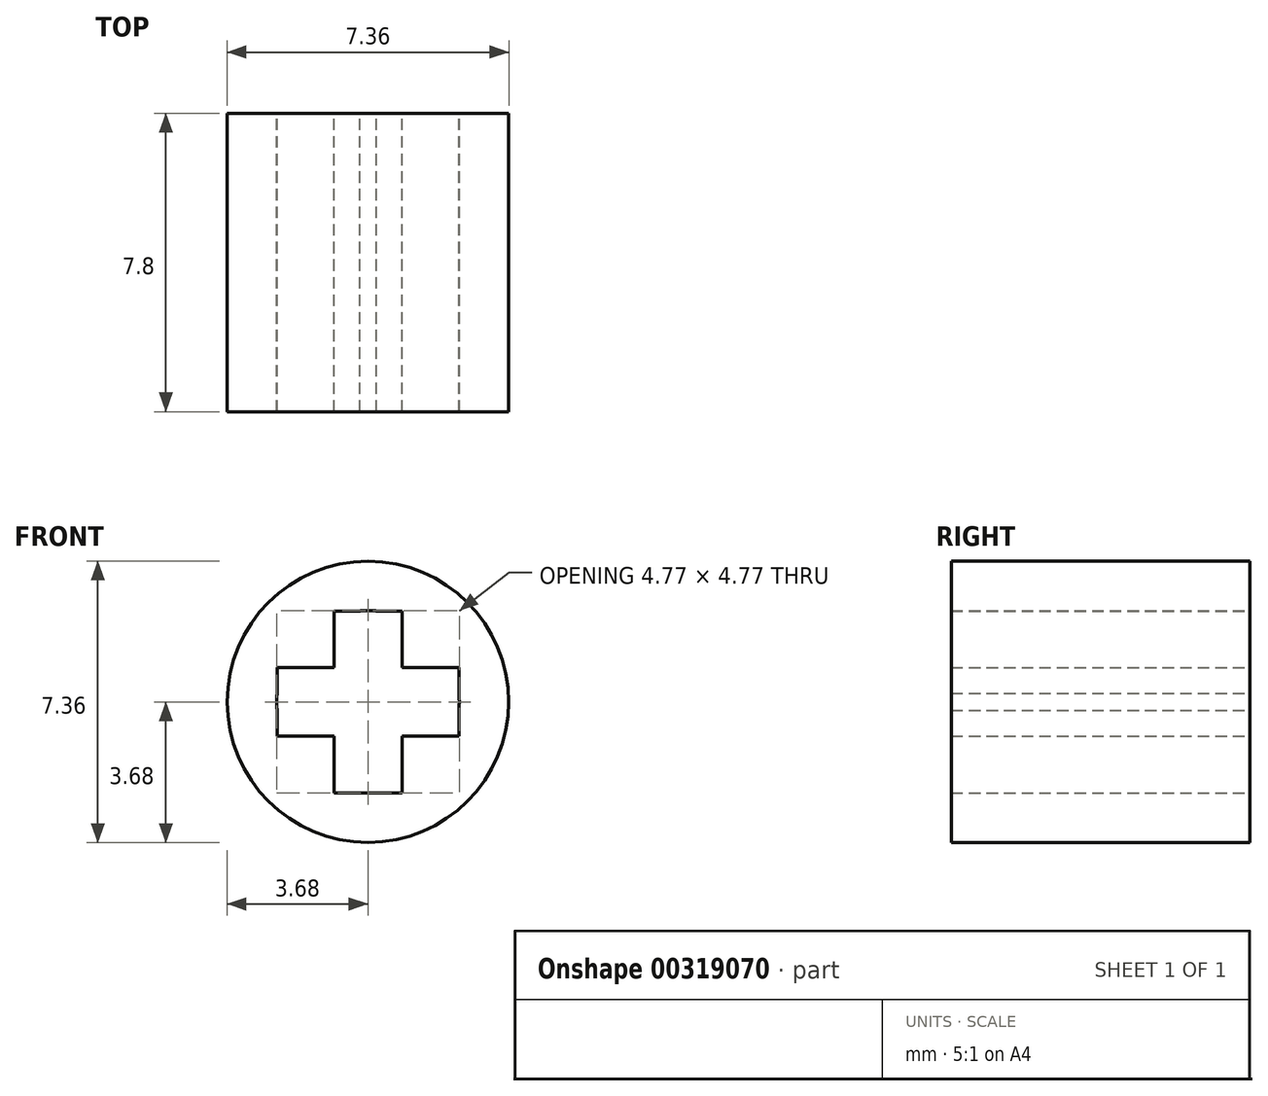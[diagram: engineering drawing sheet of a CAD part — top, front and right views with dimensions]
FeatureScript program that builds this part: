
annotation { "Feature Type Name" : "Feature", "Feature Type Description" : "" }
export const myFeature = defineFeature(function(context is Context, id is Id, definition is map)
    precondition{}
    {
        {
            var Q0;
            Q0=qCreatedBy(makeId("Front.planeOp"),FACE);
            var sketch = newSketch(context, id + "F0", { "sketchPlane" : qUnion([Q0])});
            skCircle(sketch, "E0", {"center": v(0, 0) * mm, "radius": 3.67 * mm});
            skPoint(sketch, "E1", {"position": v(-3.68, 0) * mm});
            skPoint(sketch, "E2", {"position": v(0, -2.38) * mm});
            skLineSegment(sketch, "E3.bottom", {"start": v(-2.38, 0.9) * mm, "end": v(2.38, 0.9) * mm});
            skLineSegment(sketch, "E3.top", {"start": v(-2.38, -0.89) * mm, "end": v(2.38, -0.89) * mm});
            skLineSegment(sketch, "E3.left", {"start": v(-2.38, 0.89) * mm, "end": v(-2.38, -0.89) * mm});
            skLineSegment(sketch, "E3.right", {"start": v(2.38, 0.89) * mm, "end": v(2.38, -0.89) * mm});
            skLineSegment(sketch, "E4", {"start": v(0, 0.89) * mm, "end": v(0, -0.89) * mm});
            skLineSegment(sketch, "E5.bottom", {"start": v(-0.9, 2.38) * mm, "end": v(0.9, 2.38) * mm});
            skLineSegment(sketch, "E5.top", {"start": v(-0.9, -2.37) * mm, "end": v(0.9, -2.37) * mm});
            skLineSegment(sketch, "E5.left", {"start": v(-0.9, 2.37) * mm, "end": v(-0.9, -2.37) * mm});
            skLineSegment(sketch, "E5.right", {"start": v(0.89, 2.37) * mm, "end": v(0.89, -2.37) * mm});
            skLineSegment(sketch, "E6", {"start": v(-0.9, 0) * mm, "end": v(0.9, 0) * mm});
            skCircle(sketch, "E7", {"center": v(0, 0) * mm, "radius": 2.38 * mm});
            skSolve(sketch);
        }
        {
            var Q0;
            Q0=makeQuery(id+"F0.imprint","IMPRINT",FACE,{"disambiguationData":[TD([[makeQuery(id+"F0.imprint","IMPRINT",EDGE,{"derivedFrom":sQuery(id+"F0.wireOp",EDGE,"E0")}),1.0]])]});
            var Q1;
            {var subQ0=sQuery(id+"F0.wireOp",EDGE,"E5.left");var subQ1=sQuery(id+"F0.wireOp",EDGE,"6KHPiTR4-YgFa-hmAh-xzcl-P7OBzmZ2RswI");var subQ2=makeQuery(id+"F0.imprint","INTERSECT",VERTEX,{"disambiguationData":[OD(0.0)],"derivedFrom":[subQ1,subQ0]});Q1=makeQuery(id+"F0.imprint","IMPRINT",FACE,{"disambiguationData":[TD([[makeQuery(id+"F0.imprint","IMPRINT",EDGE,{"disambiguationData":[TD([[subQ2,-1.0]])],"derivedFrom":subQ1}),-1.0]])]});}
            var Q2;
            {var subQ0=sQuery(id+"F0.wireOp",EDGE,"E5.left");var subQ1=sQuery(id+"F0.wireOp",EDGE,"6KHPiTR4-YgFa-hmAh-xzcl-P7OBzmZ2RswI");var subQ2=makeQuery(id+"F0.imprint","INTERSECT",VERTEX,{"disambiguationData":[OD(0.0)],"derivedFrom":[subQ1,subQ0]});Q2=makeQuery(id+"F0.imprint","IMPRINT",FACE,{"disambiguationData":[TD([[makeQuery(id+"F0.imprint","IMPRINT",EDGE,{"disambiguationData":[TD([[subQ2,-1.0]])],"derivedFrom":subQ1}),1.0]])]});}
            var Q3;
            {var subQ0=sQuery(id+"F0.wireOp",EDGE,"E3.left");var subQ1=sQuery(id+"F0.wireOp",EDGE,"6KHPiTR4-YgFa-hmAh-xzcl-P7OBzmZ2RswI");var subQ2=makeQuery(id+"F0.imprint","INTERSECT",VERTEX,{"disambiguationData":[OD(0.0)],"derivedFrom":[subQ1,subQ0]});Q3=makeQuery(id+"F0.imprint","IMPRINT",FACE,{"disambiguationData":[TD([[makeQuery(id+"F0.imprint","IMPRINT",EDGE,{"disambiguationData":[TD([[subQ2,-1.0]])],"derivedFrom":subQ1}),-1.0]])]});}
            var Q4;
            {var subQ0=sQuery(id+"F0.wireOp",EDGE,"E3.left");var subQ1=sQuery(id+"F0.wireOp",EDGE,"6KHPiTR4-YgFa-hmAh-xzcl-P7OBzmZ2RswI");var subQ2=makeQuery(id+"F0.imprint","INTERSECT",VERTEX,{"disambiguationData":[OD(1.0)],"derivedFrom":[subQ1,subQ0]});Q4=makeQuery(id+"F0.imprint","IMPRINT",FACE,{"disambiguationData":[TD([[makeQuery(id+"F0.imprint","IMPRINT",EDGE,{"disambiguationData":[TD([[subQ2,-1.0]])],"derivedFrom":subQ1}),-1.0]])]});}
            var Q5;
            {var subQ0=sQuery(id+"F0.wireOp",EDGE,"E3.top");var subQ1=sQuery(id+"F0.wireOp",EDGE,"6KHPiTR4-YgFa-hmAh-xzcl-P7OBzmZ2RswI");var subQ2=makeQuery(id+"F0.imprint","INTERSECT",VERTEX,{"disambiguationData":[OD(0.0)],"derivedFrom":[subQ1,subQ0]});Q5=makeQuery(id+"F0.imprint","IMPRINT",FACE,{"disambiguationData":[TD([[makeQuery(id+"F0.imprint","IMPRINT",EDGE,{"disambiguationData":[TD([[subQ2,-1.0]])],"derivedFrom":subQ1}),-1.0]])]});}
            var Q6;
            {var subQ0=sQuery(id+"F0.wireOp",EDGE,"E5.top");var subQ1=sQuery(id+"F0.wireOp",EDGE,"6KHPiTR4-YgFa-hmAh-xzcl-P7OBzmZ2RswI");var subQ2=makeQuery(id+"F0.imprint","INTERSECT",VERTEX,{"disambiguationData":[OD(0.0)],"derivedFrom":[subQ1,subQ0]});Q6=makeQuery(id+"F0.imprint","IMPRINT",FACE,{"disambiguationData":[TD([[makeQuery(id+"F0.imprint","IMPRINT",EDGE,{"disambiguationData":[TD([[subQ2,-1.0]])],"derivedFrom":subQ1}),-1.0]])]});}
            var Q7;
            {var subQ0=sQuery(id+"F0.wireOp",EDGE,"E5.top");var subQ1=sQuery(id+"F0.wireOp",EDGE,"6KHPiTR4-YgFa-hmAh-xzcl-P7OBzmZ2RswI");var subQ2=makeQuery(id+"F0.imprint","INTERSECT",VERTEX,{"disambiguationData":[OD(1.0)],"derivedFrom":[subQ1,subQ0]});Q7=makeQuery(id+"F0.imprint","IMPRINT",FACE,{"disambiguationData":[TD([[makeQuery(id+"F0.imprint","IMPRINT",EDGE,{"disambiguationData":[TD([[subQ2,-1.0]])],"derivedFrom":subQ1}),-1.0]])]});}
            var Q8;
            {var subQ0=sQuery(id+"F0.wireOp",EDGE,"E5.right");var subQ1=sQuery(id+"F0.wireOp",EDGE,"6KHPiTR4-YgFa-hmAh-xzcl-P7OBzmZ2RswI");var subQ2=makeQuery(id+"F0.imprint","INTERSECT",VERTEX,{"disambiguationData":[OD(1.0)],"derivedFrom":[subQ1,subQ0]});Q8=makeQuery(id+"F0.imprint","IMPRINT",FACE,{"disambiguationData":[TD([[makeQuery(id+"F0.imprint","IMPRINT",EDGE,{"disambiguationData":[TD([[subQ2,-1.0]])],"derivedFrom":subQ1}),-1.0]])]});}
            var Q9;
            {var subQ0=sQuery(id+"F0.wireOp",EDGE,"E3.right");var subQ1=sQuery(id+"F0.wireOp",EDGE,"6KHPiTR4-YgFa-hmAh-xzcl-P7OBzmZ2RswI");var subQ2=makeQuery(id+"F0.imprint","INTERSECT",VERTEX,{"disambiguationData":[OD(0.0)],"derivedFrom":[subQ1,subQ0]});Q9=makeQuery(id+"F0.imprint","IMPRINT",FACE,{"disambiguationData":[TD([[makeQuery(id+"F0.imprint","IMPRINT",EDGE,{"disambiguationData":[TD([[subQ2,1.0]])],"derivedFrom":subQ1}),-1.0]])]});}
            var Q10;
            {var subQ0=sQuery(id+"F0.wireOp",EDGE,"E3.bottom");var subQ1=sQuery(id+"F0.wireOp",EDGE,"6KHPiTR4-YgFa-hmAh-xzcl-P7OBzmZ2RswI");var subQ2=makeQuery(id+"F0.imprint","INTERSECT",VERTEX,{"disambiguationData":[OD(0.0)],"derivedFrom":[subQ1,subQ0]});Q10=makeQuery(id+"F0.imprint","IMPRINT",FACE,{"disambiguationData":[TD([[makeQuery(id+"F0.imprint","IMPRINT",EDGE,{"disambiguationData":[TD([[subQ2,-1.0]])],"derivedFrom":subQ1}),-1.0]])]});}
            var Q11;
            {var subQ0=sQuery(id+"F0.wireOp",EDGE,"E5.bottom");var subQ1=sQuery(id+"F0.wireOp",EDGE,"6KHPiTR4-YgFa-hmAh-xzcl-P7OBzmZ2RswI");var subQ2=makeQuery(id+"F0.imprint","INTERSECT",VERTEX,{"disambiguationData":[OD(0.0)],"derivedFrom":[subQ1,subQ0]});Q11=makeQuery(id+"F0.imprint","IMPRINT",FACE,{"disambiguationData":[TD([[makeQuery(id+"F0.imprint","IMPRINT",EDGE,{"disambiguationData":[TD([[subQ2,-1.0]])],"derivedFrom":subQ1}),-1.0]])]});}
            var Q12;
            {var subQ0=sQuery(id+"F0.wireOp",EDGE,"E5.bottom");var subQ1=sQuery(id+"F0.wireOp",EDGE,"6KHPiTR4-YgFa-hmAh-xzcl-P7OBzmZ2RswI");var subQ2=makeQuery(id+"F0.imprint","INTERSECT",VERTEX,{"disambiguationData":[OD(1.0)],"derivedFrom":[subQ1,subQ0]});Q12=makeQuery(id+"F0.imprint","IMPRINT",FACE,{"disambiguationData":[TD([[makeQuery(id+"F0.imprint","IMPRINT",EDGE,{"disambiguationData":[TD([[subQ2,-1.0]])],"derivedFrom":subQ1}),-1.0]])]});}
            var Q13;
            Q13=makeQuery(id+"F0.imprint","IMPRINT",FACE,{"disambiguationData":[TD([[makeQuery(id+"F0.imprint","IMPRINT",EDGE,{"derivedFrom":sQuery(id+"F0.wireOp",EDGE,"OIfHmx78-MSyi-a2KD-d5bX-9mKDEIvE6SVB")}),1.0]])]});
            var Q14;
            {var subQ0=sQuery(id+"F0.wireOp",EDGE,"E3.top");var subQ1=sQuery(id+"F0.wireOp",EDGE,"6KHPiTR4-YgFa-hmAh-xzcl-P7OBzmZ2RswI");var subQ2=makeQuery(id+"F0.imprint","INTERSECT",VERTEX,{"disambiguationData":[OD(0.0)],"derivedFrom":[subQ1,subQ0]});Q14=makeQuery(id+"F0.imprint","IMPRINT",FACE,{"disambiguationData":[TD([[makeQuery(id+"F0.imprint","IMPRINT",EDGE,{"disambiguationData":[TD([[subQ2,-1.0]])],"derivedFrom":subQ1}),1.0]])]});}
            var Q15;
            {var subQ0=sQuery(id+"F0.wireOp",EDGE,"E5.right");var subQ1=sQuery(id+"F0.wireOp",EDGE,"6KHPiTR4-YgFa-hmAh-xzcl-P7OBzmZ2RswI");var subQ2=makeQuery(id+"F0.imprint","INTERSECT",VERTEX,{"disambiguationData":[OD(1.0)],"derivedFrom":[subQ1,subQ0]});Q15=makeQuery(id+"F0.imprint","IMPRINT",FACE,{"disambiguationData":[TD([[makeQuery(id+"F0.imprint","IMPRINT",EDGE,{"disambiguationData":[TD([[subQ2,-1.0]])],"derivedFrom":subQ1}),1.0]])]});}
            var Q16;
            {var subQ0=sQuery(id+"F0.wireOp",EDGE,"E3.bottom");var subQ1=sQuery(id+"F0.wireOp",EDGE,"6KHPiTR4-YgFa-hmAh-xzcl-P7OBzmZ2RswI");var subQ2=makeQuery(id+"F0.imprint","INTERSECT",VERTEX,{"disambiguationData":[OD(0.0)],"derivedFrom":[subQ1,subQ0]});Q16=makeQuery(id+"F0.imprint","IMPRINT",FACE,{"disambiguationData":[TD([[makeQuery(id+"F0.imprint","IMPRINT",EDGE,{"disambiguationData":[TD([[subQ2,-1.0]])],"derivedFrom":subQ1}),1.0]])]});}
            extrude(context, id + "F1", {"entities" : qUnion([Q0, Q1, Q2, Q3, Q4, Q5, Q6, Q7, Q8, Q9, Q10, Q11, Q12, Q13, Q14, Q15, Q16]), "depth" : 7.8 * mm});
        }
        {
            var Q0;
            {var subQ0=sQuery(id+"F0.wireOp",EDGE,"E7");var subQ1=sQuery(id+"F0.wireOp",EDGE,"E3.bottom");var subQ2=makeQuery(id+"F0.imprint","INTERSECT",VERTEX,{"disambiguationData":[OD(0.0)],"derivedFrom":[subQ1,subQ0]});Q0=makeQuery(id+"F0.imprint","IMPRINT",FACE,{"disambiguationData":[TD([[makeQuery(id+"F0.imprint","IMPRINT",EDGE,{"disambiguationData":[TD([[subQ2,-1.0]])],"derivedFrom":subQ1}),1.0]])]});}
            var Q1;
            {var subQ0=sQuery(id+"F0.wireOp",EDGE,"E5.right");var subQ1=sQuery(id+"F0.wireOp",EDGE,"E3.bottom");var subQ2=makeQuery(id+"F0.imprint","INTERSECT",VERTEX,{"derivedFrom":[subQ1,subQ0]});Q1=makeQuery(id+"F0.imprint","IMPRINT",FACE,{"disambiguationData":[TD([[makeQuery(id+"F0.imprint","IMPRINT",EDGE,{"disambiguationData":[TD([[subQ2,-1.0]])],"derivedFrom":subQ1}),1.0]])]});}
            var Q2;
            {var subQ0=sQuery(id+"F0.wireOp",EDGE,"E7");var subQ1=sQuery(id+"F0.wireOp",EDGE,"E3.top");var subQ2=makeQuery(id+"F0.imprint","INTERSECT",VERTEX,{"disambiguationData":[OD(0.0)],"derivedFrom":[subQ1,subQ0]});Q2=makeQuery(id+"F0.imprint","IMPRINT",FACE,{"disambiguationData":[TD([[makeQuery(id+"F0.imprint","IMPRINT",EDGE,{"disambiguationData":[TD([[subQ2,-1.0]])],"derivedFrom":subQ1}),-1.0]])]});}
            var Q3;
            {var subQ0=sQuery(id+"F0.wireOp",EDGE,"E5.right");var subQ1=sQuery(id+"F0.wireOp",EDGE,"E3.top");var subQ2=makeQuery(id+"F0.imprint","INTERSECT",VERTEX,{"derivedFrom":[subQ1,subQ0]});Q3=makeQuery(id+"F0.imprint","IMPRINT",FACE,{"disambiguationData":[TD([[makeQuery(id+"F0.imprint","IMPRINT",EDGE,{"disambiguationData":[TD([[subQ2,-1.0]])],"derivedFrom":subQ1}),-1.0]])]});}
            extrude(context, id + "F2", {"entities" : qUnion([Q0, Q1, Q2, Q3]), "operationType" : NewBodyOperationType.ADD, "depth" : 7.8 * mm});
        }
    });
